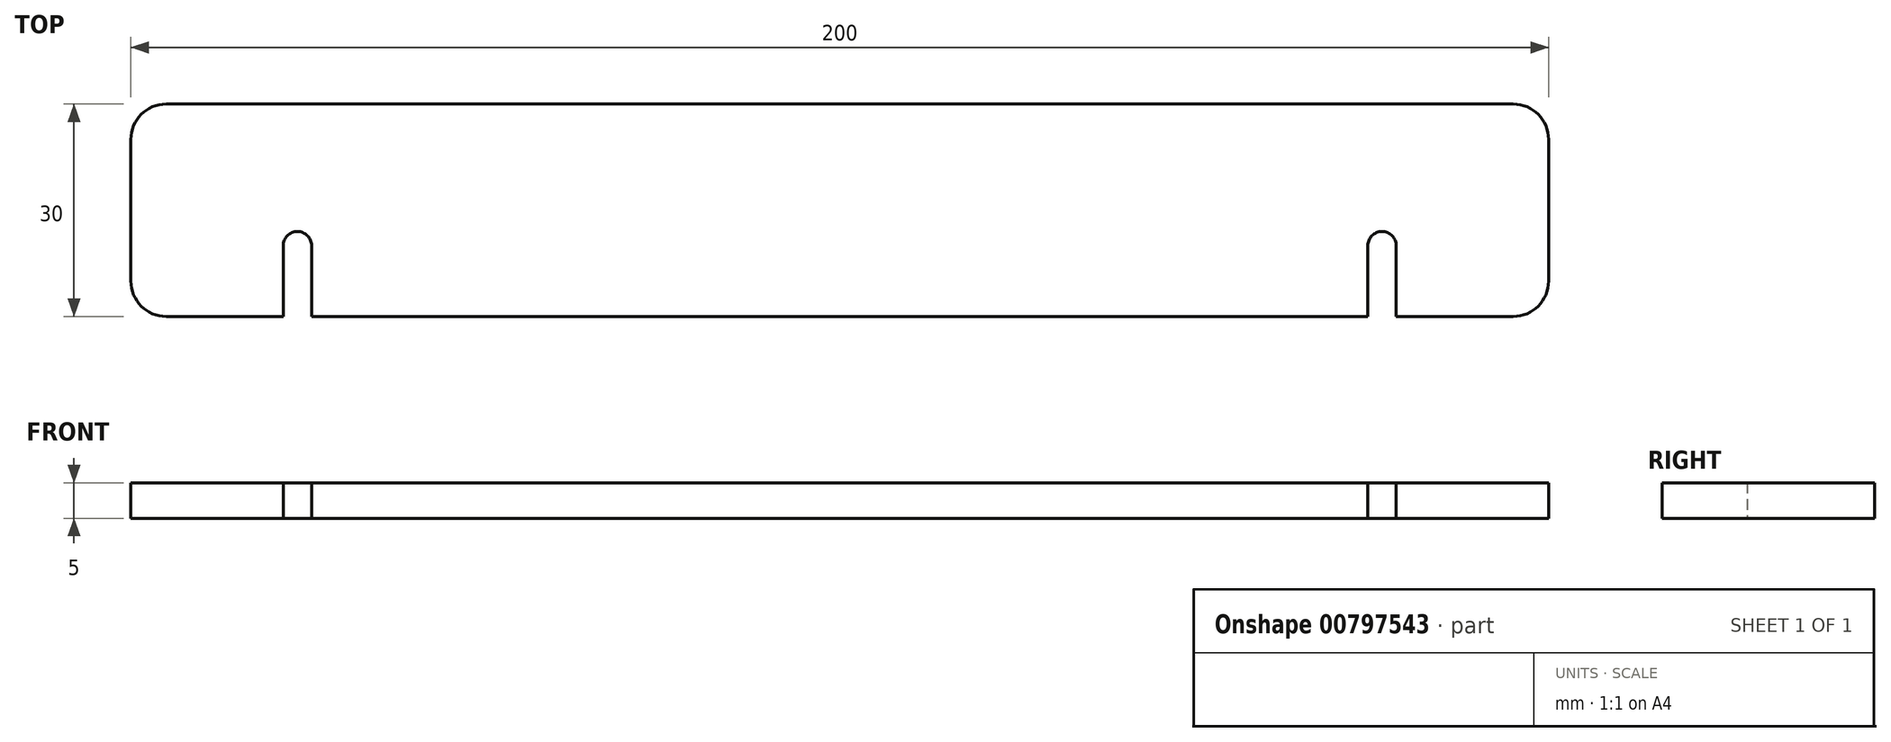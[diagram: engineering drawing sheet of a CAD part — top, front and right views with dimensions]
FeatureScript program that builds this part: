
annotation { "Feature Type Name" : "Feature", "Feature Type Description" : "" }
export const myFeature = defineFeature(function(context is Context, id is Id, definition is map)
    precondition{}
    {
        {
            var Q0;
            Q0=qCreatedBy(makeId("Top.planeOp"),FACE);
            var sketch = newSketch(context, id + "F0", { "sketchPlane" : qUnion([Q0])});
            skLineSegment(sketch, "E0.bottom", {"start": v(-95, 15) * mm, "end": v(95, 15) * mm});
            skLineSegment(sketch, "E0.left", {"start": v(-100, 10) * mm, "end": v(-100, -10) * mm});
            skLineSegment(sketch, "E0.right", {"start": v(100, 10) * mm, "end": v(100, -10) * mm});
            skLineSegment(sketch, "E1", {"start": v(78.5, -15) * mm, "end": v(78.5, -5) * mm});
            skLineSegment(sketch, "E2", {"start": v(74.5, -15) * mm, "end": v(74.5, -5) * mm});
            skArc(sketch, "E3", {"start": v(78.5, -5) * mm, "mid": v(76.5, -3) * mm, "end": v(74.5, -5) * mm});
            skPoint(sketch, "E4", {"position": v(100, 0) * mm});
            skLineSegment(sketch, "E5", {"start": v(78.5, -15) * mm, "end": v(95, -15) * mm});
            skLineSegment(sketch, "E6", {"start": v(-95, -15) * mm, "end": v(-78.5, -15) * mm});
            skLineSegment(sketch, "E7", {"start": v(-78.5, -15) * mm, "end": v(-78.5, -5) * mm});
            skLineSegment(sketch, "E8", {"start": v(74.5, -15) * mm, "end": v(-74.5, -15) * mm});
            skLineSegment(sketch, "E9", {"start": v(-74.5, -15) * mm, "end": v(-74.5, -5) * mm});
            skArc(sketch, "E10", {"start": v(-74.5, -5) * mm, "mid": v(-76.5, -3) * mm, "end": v(-78.5, -5) * mm});
            skPoint(sketch, "E11", {"position": v(-100, 0) * mm});
            skLineSegment(sketch, "E12", {"start": v(74.5, -15) * mm, "end": v(78.5, -15) * mm, "construction": true});
            skLineSegment(sketch, "E13", {"start": v(-78.5, -15) * mm, "end": v(-74.5, -15) * mm, "construction": true});
            skPoint(sketch, "E14.visualSharp", {"position": v(100, 15) * mm});
            skArc(sketch, "E14.filletArc", {"start": v(100, 10) * mm, "mid": v(98.54, 13.54) * mm, "end": v(95, 15) * mm});
            skPoint(sketch, "E15.visualSharp", {"position": v(-100, 15) * mm});
            skArc(sketch, "E15.filletArc", {"start": v(-95, 15) * mm, "mid": v(-98.54, 13.54) * mm, "end": v(-100, 10) * mm});
            skPoint(sketch, "E16.visualSharp", {"position": v(-100, -15) * mm});
            skArc(sketch, "E16.filletArc", {"start": v(-100, -10) * mm, "mid": v(-98.54, -13.54) * mm, "end": v(-95, -15) * mm});
            skPoint(sketch, "E17.visualSharp", {"position": v(100, -15) * mm});
            skArc(sketch, "E17.filletArc", {"start": v(95, -15) * mm, "mid": v(98.54, -13.54) * mm, "end": v(100, -10) * mm});
            skSolve(sketch);
        }
        {
            var Q0;
            Q0 = qSketchRegion(id + "F0", true);
            extrude(context, id + "F1", {"entities" : qUnion([Q0]), "depth" : 5 * mm, "offsetDistance" : 25 * mm});
        }
    });
